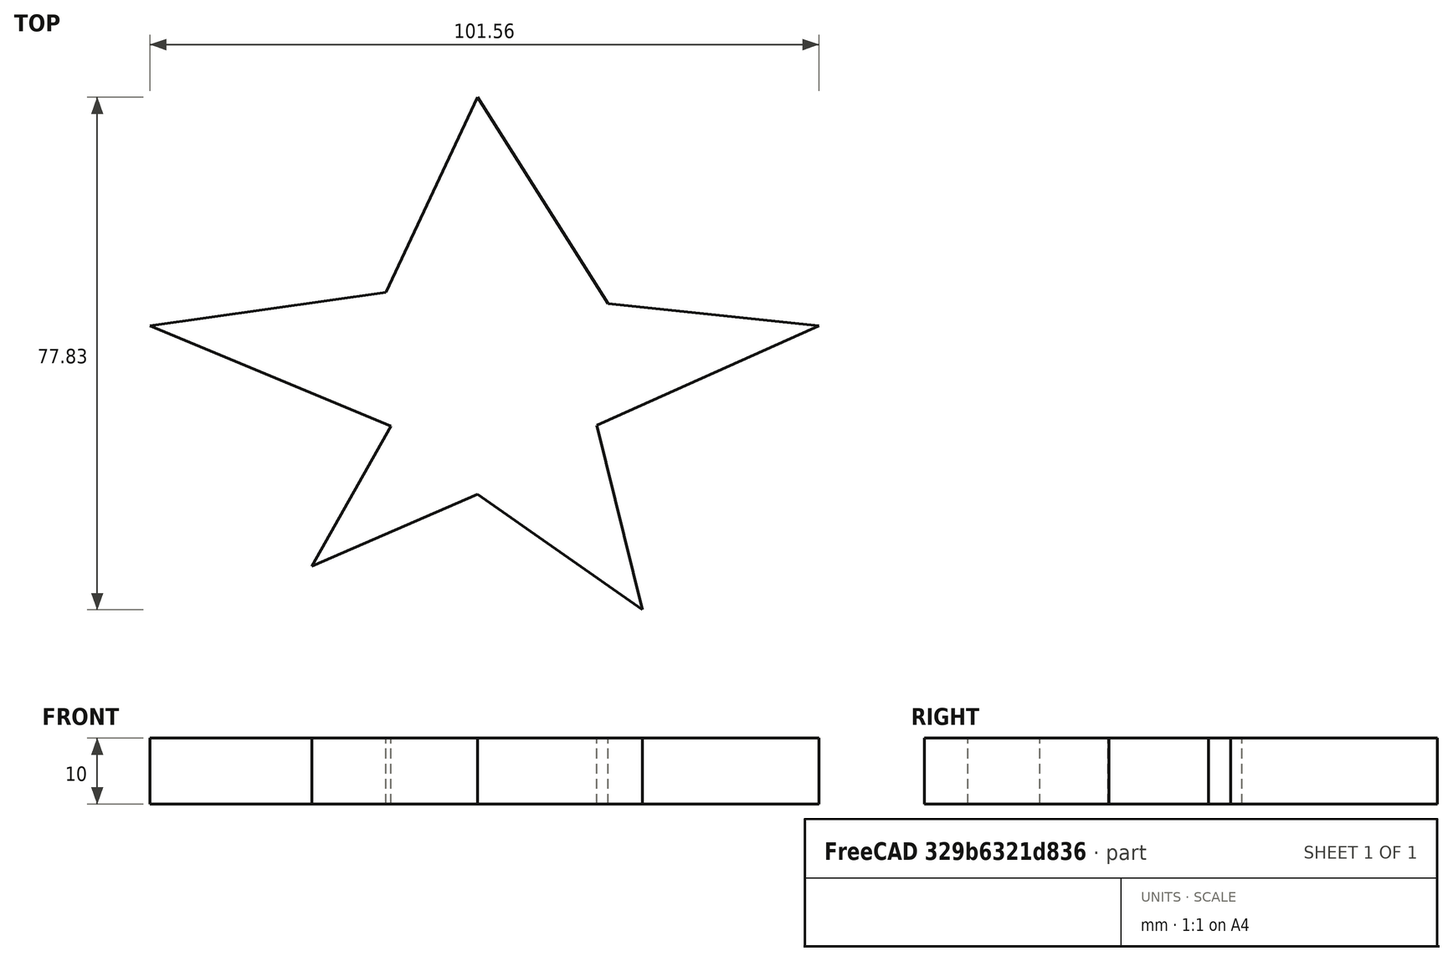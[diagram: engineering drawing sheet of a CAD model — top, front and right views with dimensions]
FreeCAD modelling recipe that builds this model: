
FCSTD DOCUMENT  (FreeCAD 0.21R33694 (Git))
Label: OJT1_T16P01.estrella
License: All rights reserved
LicenseURL: http://en.wikipedia.org/wiki/All_rights_reserved
objects: Sketcher::SketchObject×1, PartDesign::Pad×1, PartDesign::Body×1
note: 4 computed .brp shape members not serialized (recipe doc carries the construction recipe); baked Part::Feature solids carry a one-line shape summary decoded from their .brp

FEATURE [Sketcher::SketchObject] Sketch
  FullyConstrained = false
  MapMode = 5
  Support = -> [XY_Plane]
  sketch-geometry (10):
    g0: LineSegment StartX=0 StartY=39.0565 StartZ=0 EndX=19.8096 EndY=7.71314 EndZ=0
    g1: LineSegment StartX=19.8096 StartY=7.71314 StartZ=0 EndX=51.8103 EndY=4.32564 EndZ=0
    g2: LineSegment StartX=51.8103 StartY=4.32564 StartZ=0 EndX=18.0559 EndY=-10.7433 EndZ=0
    g3: LineSegment StartX=18.0559 StartY=-10.7433 StartZ=0 EndX=24.9876 EndY=-38.7715 EndZ=0
    g4: LineSegment StartX=24.9876 StartY=-38.7715 StartZ=0 EndX=0 EndY=-21.2192 EndZ=0
    g5: LineSegment StartX=0 StartY=-21.2192 StartZ=0 EndX=-25.1787 EndY=-32.1788 EndZ=0
    g6: LineSegment StartX=-25.1787 StartY=-32.1788 StartZ=0 EndX=-13.1533 EndY=-10.8928 EndZ=0
    g7: LineSegment StartX=-13.1533 StartY=-10.8928 StartZ=0 EndX=-49.7543 EndY=4.32564 EndZ=0
    g8: LineSegment StartX=-49.7543 StartY=4.32564 StartZ=0 EndX=-13.8902 EndY=9.44908 EndZ=0
    g9: LineSegment StartX=-13.8902 StartY=9.44908 StartZ=0 EndX=0 EndY=39.0565 EndZ=0
  constraints (12):
    c: PointOnObject(g0,g-2)
    c: Coincident(g0,g1)
    c: Coincident(g1,g2)
    c: Coincident(g2,g3)
    c: Coincident(g3,g4)
    c: PointOnObject(g4,g-2)
    c: Coincident(g4,g5)
    c: Coincident(g5,g6)
    c: Coincident(g6,g7)
    c: Coincident(g7,g8)
    c: Coincident(g8,g9)
    c: Coincident(g9,g0)
FEATURE [PartDesign::Pad] Pad
  Direction = (0,0,1)
  Length = 10
  Length2 = 10
  Profile = -> Sketch
  ReferenceAxis = -> Sketch [N_Axis]
  Refine = true
  Type = 0
FEATURE [PartDesign::Body] Body
  Group = -> [Sketch,Pad]
  Origin = -> Origin
  Tip = -> Pad
